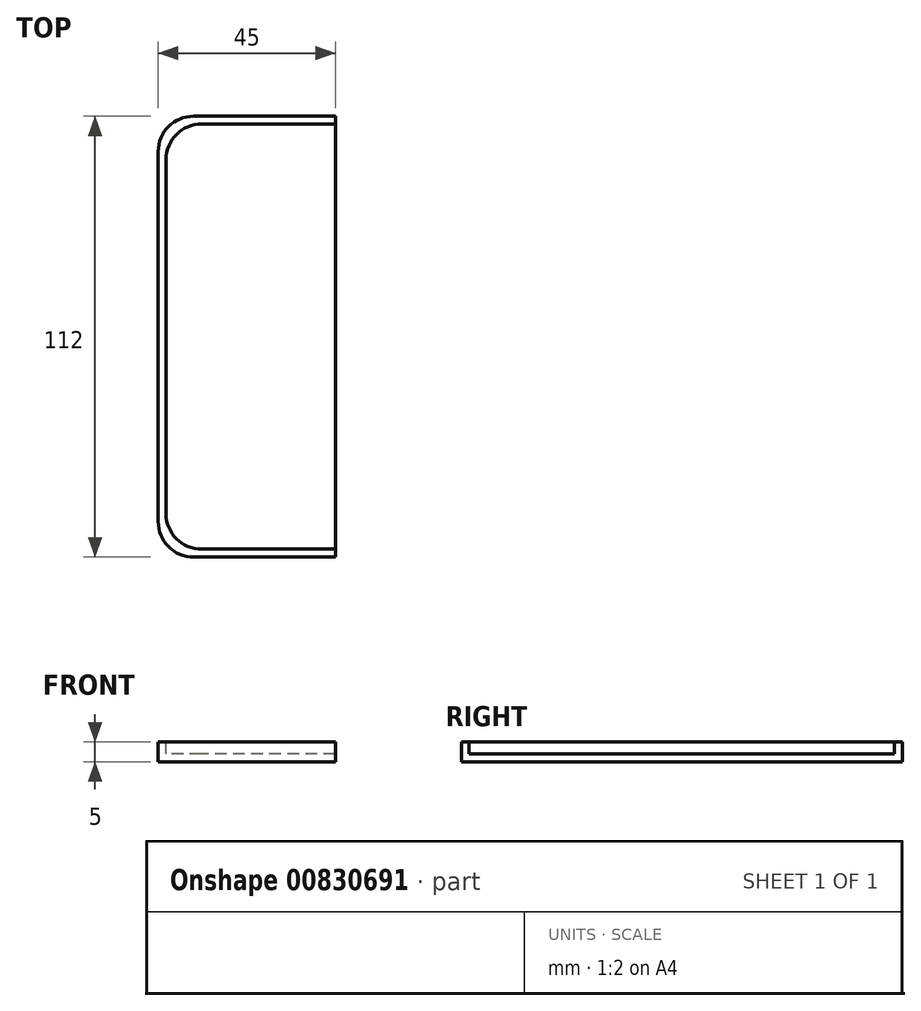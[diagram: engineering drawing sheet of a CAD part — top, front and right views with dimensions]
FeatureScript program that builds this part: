
annotation { "Feature Type Name" : "Feature", "Feature Type Description" : "" }
export const myFeature = defineFeature(function(context is Context, id is Id, definition is map)
    precondition{}
    {
        {
            var Q0;
            Q0=qCreatedBy(makeId("Top.planeOp"),FACE);
            var sketch = newSketch(context, id + "F0", { "sketchPlane" : qUnion([Q0])});
            skLineSegment(sketch, "E0.bottom", {"start": v(-86, -56) * mm, "end": v(-50, -56) * mm});
            skLineSegment(sketch, "E0.top", {"start": v(-86, 56) * mm, "end": v(-50, 56) * mm});
            skLineSegment(sketch, "E0.left", {"start": v(-95, -47) * mm, "end": v(-95, 47) * mm});
            skPoint(sketch, "E1.visualSharp", {"position": v(-95, -56) * mm});
            skArc(sketch, "E1.filletArc", {"start": v(-95, -47) * mm, "mid": v(-92.36, -53.36) * mm, "end": v(-86, -56) * mm});
            skPoint(sketch, "E2.visualSharp", {"position": v(-95, 56) * mm});
            skArc(sketch, "E2.filletArc", {"start": v(-86, 56) * mm, "mid": v(-92.36, 53.36) * mm, "end": v(-95, 47) * mm});
            skLineSegment(sketch, "E3", {"start": v(-50, -56) * mm, "end": v(-50, 56) * mm});
            skSolve(sketch);
        }
        {
            var Q0;
            Q0 = qSketchRegion(id + "F0", true);
            extrude(context, id + "F1", {"entities" : qUnion([Q0]), "depth" : 5 * mm, "offsetDistance" : 25 * mm});
        }
        {
            var Q0;
            Q0=makeQuery(id+"F1.opExtrude","CAP_FACE",FACE,{"disambiguationData":[OSD([sQuery(id+"F0.wireOp",EDGE,"E0.bottom"),sQuery(id+"F0.wireOp",EDGE,"E0.top"),sQuery(id+"F0.wireOp",EDGE,"E0.left"),sQuery(id+"F0.wireOp",EDGE,"E1.filletArc"),sQuery(id+"F0.wireOp",EDGE,"E2.filletArc"),sQuery(id+"F0.wireOp",EDGE,"E3")])],"isStart":false});
            var sketch = newSketch(context, id + "F2", { "sketchPlane" : qUnion([Q0])});
            skLineSegment(sketch, "E4", {"start": v(-50, 54) * mm, "end": v(-84, 54) * mm});
            skLineSegment(sketch, "E5", {"start": v(-50, -54) * mm, "end": v(-84, -54) * mm});
            skLineSegment(sketch, "E6", {"start": v(-93, 45) * mm, "end": v(-93, -45) * mm});
            skLineSegment(sketch, "E7", {"start": v(-50, -54) * mm, "end": v(-50, 54) * mm});
            skArc(sketch, "E8.filletArc", {"start": v(-84, 54) * mm, "mid": v(-90.36, 51.36) * mm, "end": v(-93, 45) * mm});
            skArc(sketch, "E9.filletArc", {"start": v(-93, -45) * mm, "mid": v(-90.36, -51.36) * mm, "end": v(-84, -54) * mm});
            skSolve(sketch);
        }
        {
            var Q0;
            Q0=makeQuery(id+"F2.imprint","IMPRINT",FACE,{"disambiguationData":[TD([[makeQuery(id+"F2.imprint","IMPRINT",EDGE,{"derivedFrom":sQuery(id+"F2.wireOp",EDGE,"E4")}),1.0]])]});
            extrude(context, id + "F3", {"entities" : qUnion([Q0]), "operationType" : NewBodyOperationType.REMOVE, "oppositeDirection" : true, "depth" : 3 * mm, "offsetDistance" : 25 * mm});
        }
    });
